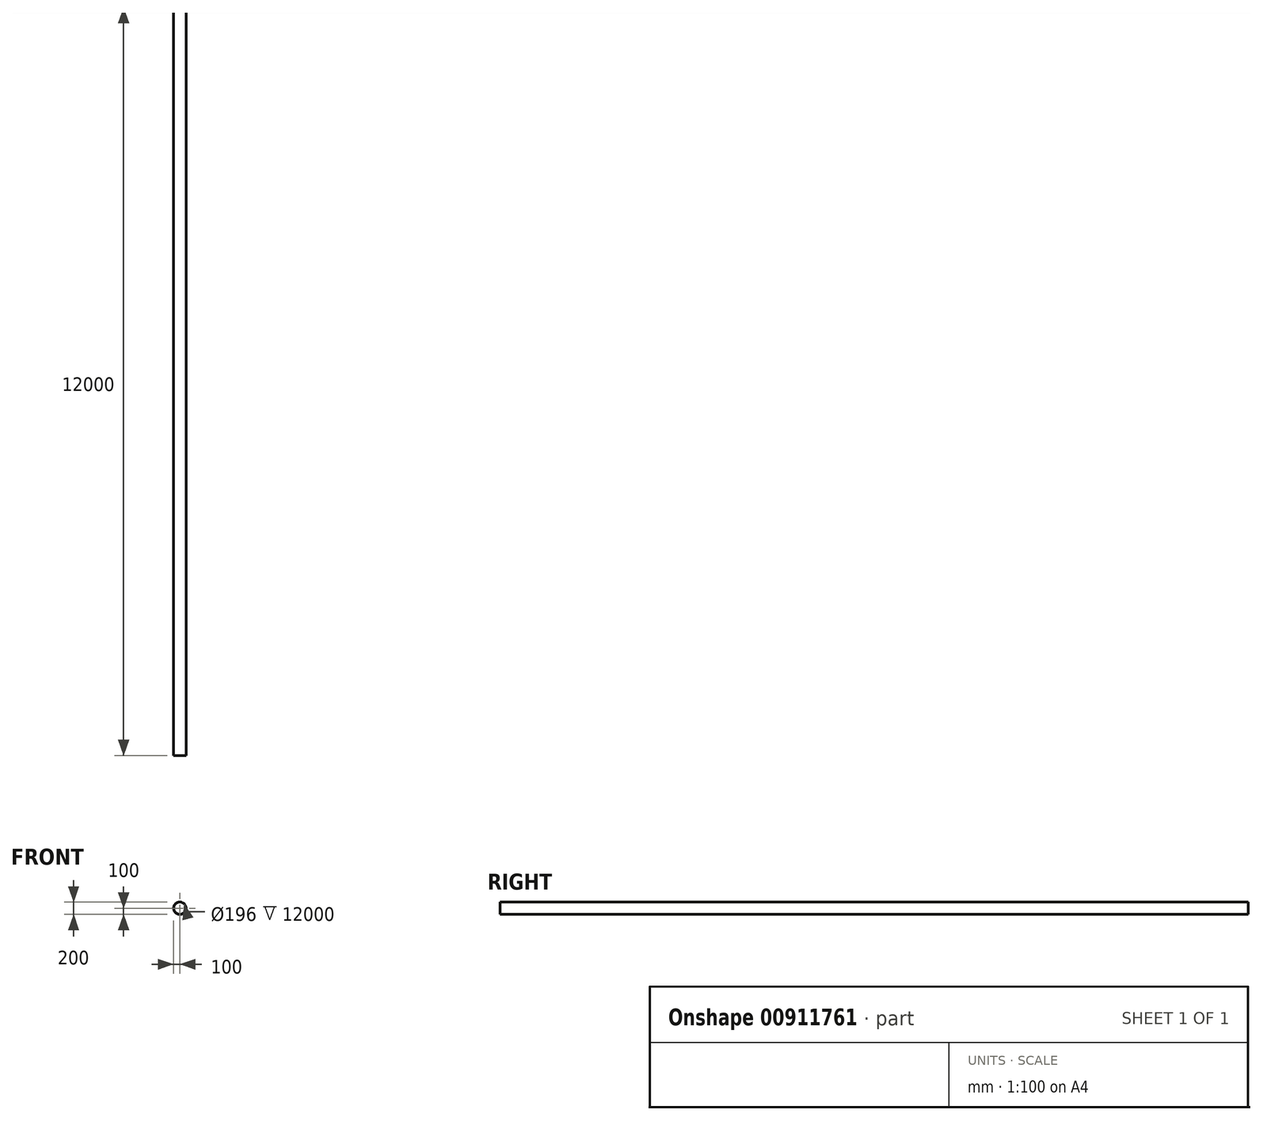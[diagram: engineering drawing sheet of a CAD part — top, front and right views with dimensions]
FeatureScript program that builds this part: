
annotation { "Feature Type Name" : "Feature", "Feature Type Description" : "" }
export const myFeature = defineFeature(function(context is Context, id is Id, definition is map)
    precondition{}
    {
        {
            var Q0;
            Q0=qCreatedBy(makeId("Front.planeOp"),FACE);
            var sketch = newSketch(context, id + "F0", { "sketchPlane" : qUnion([Q0])});
            skCircle(sketch, "E0", {"center": v(0, 0) * mm, "radius": 100 * mm});
            skCircle(sketch, "E1", {"center": v(0, 0) * mm, "radius": 98 * mm});
            skSolve(sketch);
        }
        {
            var Q0;
            Q0=makeQuery(id+"F0.imprint","IMPRINT",FACE,{"disambiguationData":[TD([[makeQuery(id+"F0.imprint","IMPRINT",EDGE,{"derivedFrom":sQuery(id+"F0.wireOp",EDGE,"E0")}),1.0]])]});
            extrude(context, id + "F1", {"entities" : qUnion([Q0]), "depth" : 12000 * mm, "offsetDistance" : 25 * mm});
        }
    });
